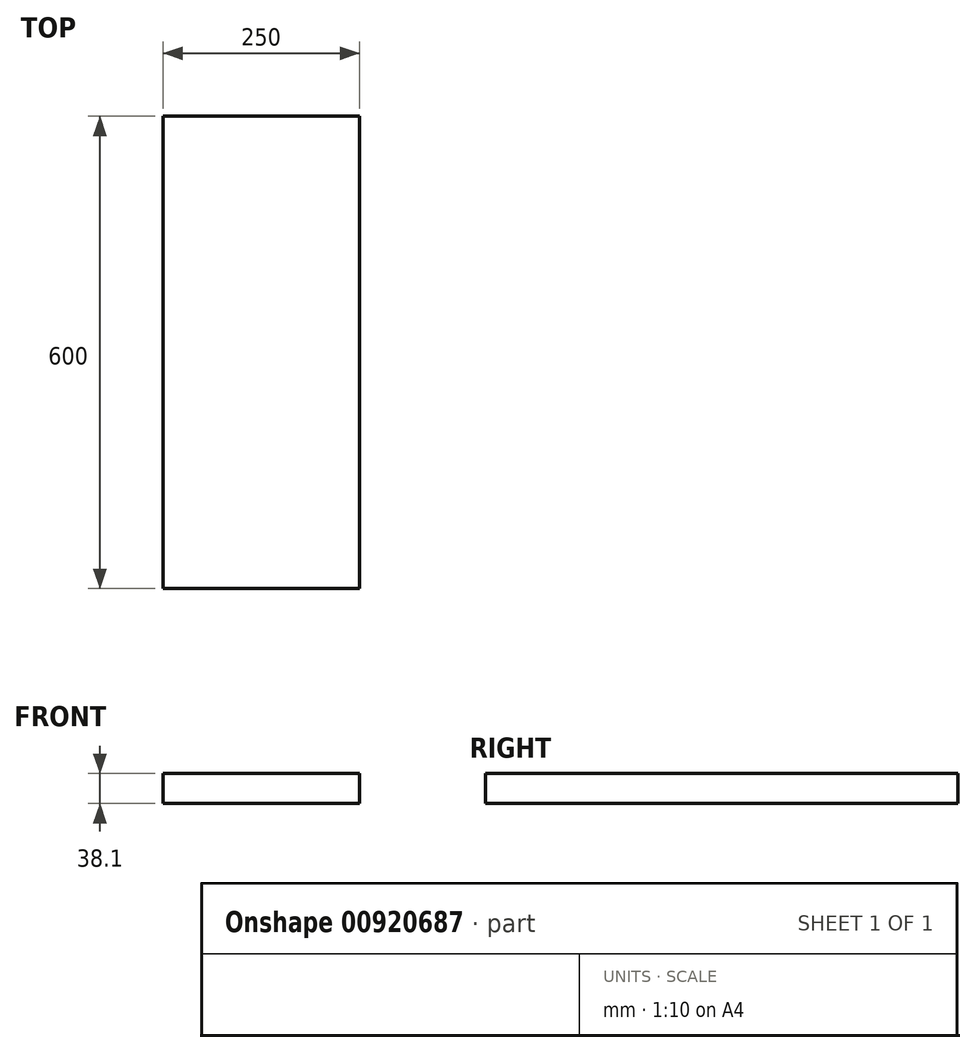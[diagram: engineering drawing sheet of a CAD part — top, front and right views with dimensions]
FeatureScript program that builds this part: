
annotation { "Feature Type Name" : "Feature", "Feature Type Description" : "" }
export const myFeature = defineFeature(function(context is Context, id is Id, definition is map)
    precondition{}
    {
        {
            var Q0;
            Q0=qCreatedBy(makeId("Top.planeOp"),FACE);
            var sketch = newSketch(context, id + "F0", { "sketchPlane" : qUnion([Q0])});
            skLineSegment(sketch, "E0.bottom", {"start": v(0, 0) * mm, "end": v(250, 0) * mm});
            skLineSegment(sketch, "E0.top", {"start": v(0, 600) * mm, "end": v(250, 600) * mm});
            skLineSegment(sketch, "E0.left", {"start": v(0, 0) * mm, "end": v(0, 600) * mm});
            skLineSegment(sketch, "E0.right", {"start": v(250, 0) * mm, "end": v(250, 600) * mm});
            skSolve(sketch);
        }
        {
            var Q0;
            Q0=makeQuery(id+"F0.imprint","IMPRINT",FACE,{"disambiguationData":[TD([[makeQuery(id+"F0.imprint","IMPRINT",EDGE,{"derivedFrom":sQuery(id+"F0.wireOp",EDGE,"E0.bottom")}),1.0]])]});
            extrude(context, id + "F1", {"entities" : qUnion([Q0]), "depth" : 38.1 * mm, "offsetDistance" : 25 * mm});
        }
    });
